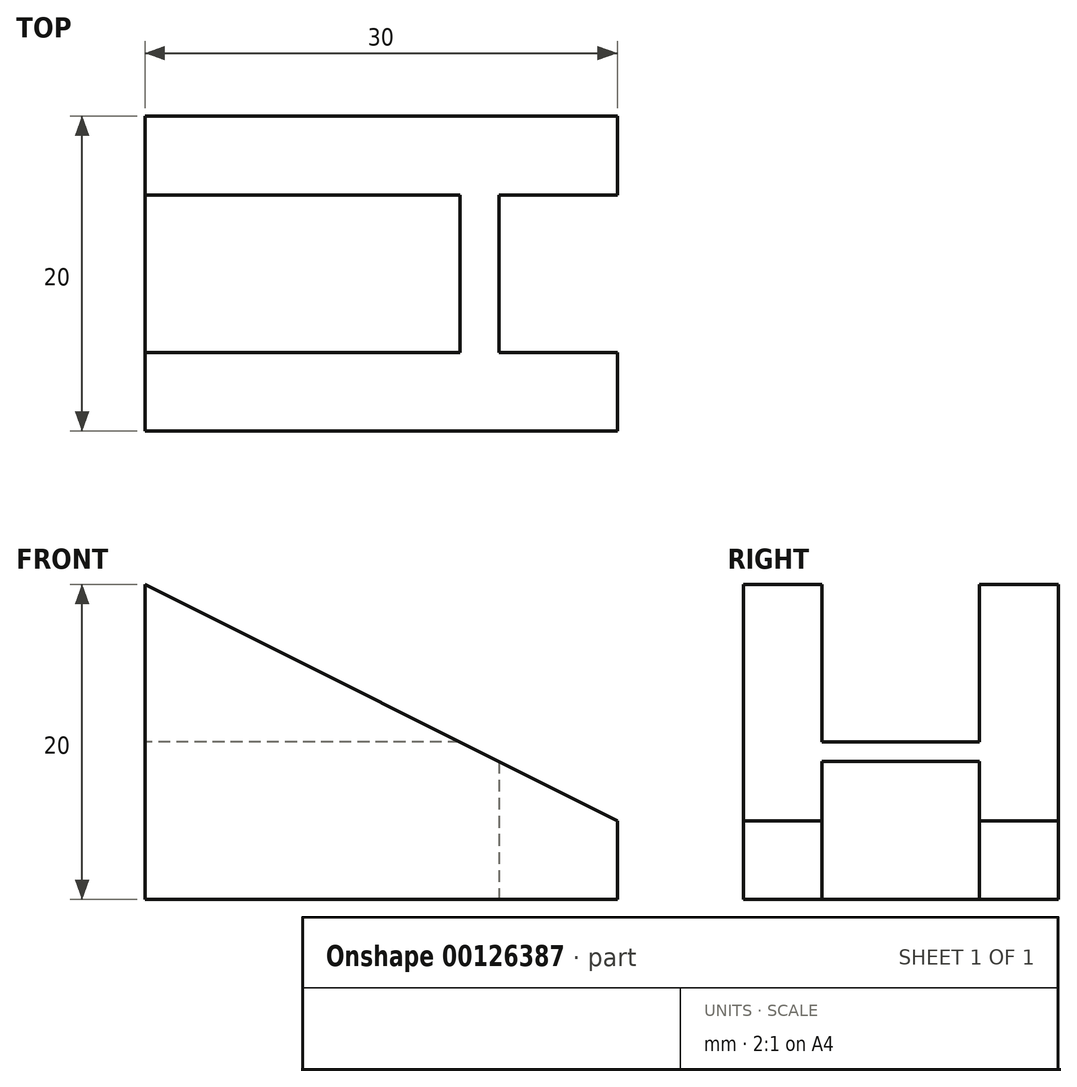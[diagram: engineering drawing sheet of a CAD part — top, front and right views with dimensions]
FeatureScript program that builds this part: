
annotation { "Feature Type Name" : "Feature", "Feature Type Description" : "" }
export const myFeature = defineFeature(function(context is Context, id is Id, definition is map)
    precondition{}
    {
        {
            var Q0;
            Q0=qCreatedBy(makeId("Front.planeOp"),FACE);
            var sketch = newSketch(context, id + "F0", { "sketchPlane" : qUnion([Q0])});
            skLineSegment(sketch, "E0", {"start": v(0, 0) * mm, "end": v(0, 20) * mm});
            skLineSegment(sketch, "E1", {"start": v(0, 20) * mm, "end": v(30, 5) * mm});
            skLineSegment(sketch, "E2", {"start": v(30, 5) * mm, "end": v(30, 0) * mm});
            skLineSegment(sketch, "E3", {"start": v(30, 0) * mm, "end": v(0, 0) * mm});
            skSolve(sketch);
        }
        {
            var Q0;
            Q0 = qSketchRegion(id + "F0", true);
            extrude(context, id + "F1", {"entities" : qUnion([Q0]), "oppositeDirection" : true, "depth" : 20 * mm});
        }
        {
            var Q0;
            Q0=qCreatedBy(makeId("Right.planeOp"),FACE);
            var sketch = newSketch(context, id + "F2", { "sketchPlane" : qUnion([Q0])});
            skLineSegment(sketch, "E4.bottom", {"start": v(5, 20) * mm, "end": v(15, 20) * mm});
            skLineSegment(sketch, "E4.top", {"start": v(5, 10) * mm, "end": v(15, 10) * mm});
            skLineSegment(sketch, "E4.left", {"start": v(5, 20) * mm, "end": v(5, 10) * mm});
            skLineSegment(sketch, "E4.right", {"start": v(15, 20) * mm, "end": v(15, 10) * mm});
            skSolve(sketch);
        }
        {
            var Q0;
            Q0 = qSketchRegion(id + "F2", true);
            extrude(context, id + "F3", {"entities" : qUnion([Q0]), "operationType" : NewBodyOperationType.REMOVE, "depth" : 25 * mm});
        }
        {
            var Q0;
            Q0=qCreatedBy(makeId("Top.planeOp"),FACE);
            var sketch = newSketch(context, id + "F4", { "sketchPlane" : qUnion([Q0])});
            skLineSegment(sketch, "E5.bottom", {"start": v(22.5, 15) * mm, "end": v(30, 15) * mm});
            skLineSegment(sketch, "E5.top", {"start": v(22.5, 5) * mm, "end": v(30, 5) * mm});
            skLineSegment(sketch, "E5.left", {"start": v(22.5, 15) * mm, "end": v(22.5, 5) * mm});
            skLineSegment(sketch, "E5.right", {"start": v(30, 15) * mm, "end": v(30, 5) * mm});
            skSolve(sketch);
        }
        {
            var Q0;
            Q0 = qSketchRegion(id + "F4", true);
            extrude(context, id + "F5", {"entities" : qUnion([Q0]), "operationType" : NewBodyOperationType.REMOVE, "depth" : 25 * mm});
        }
    });
